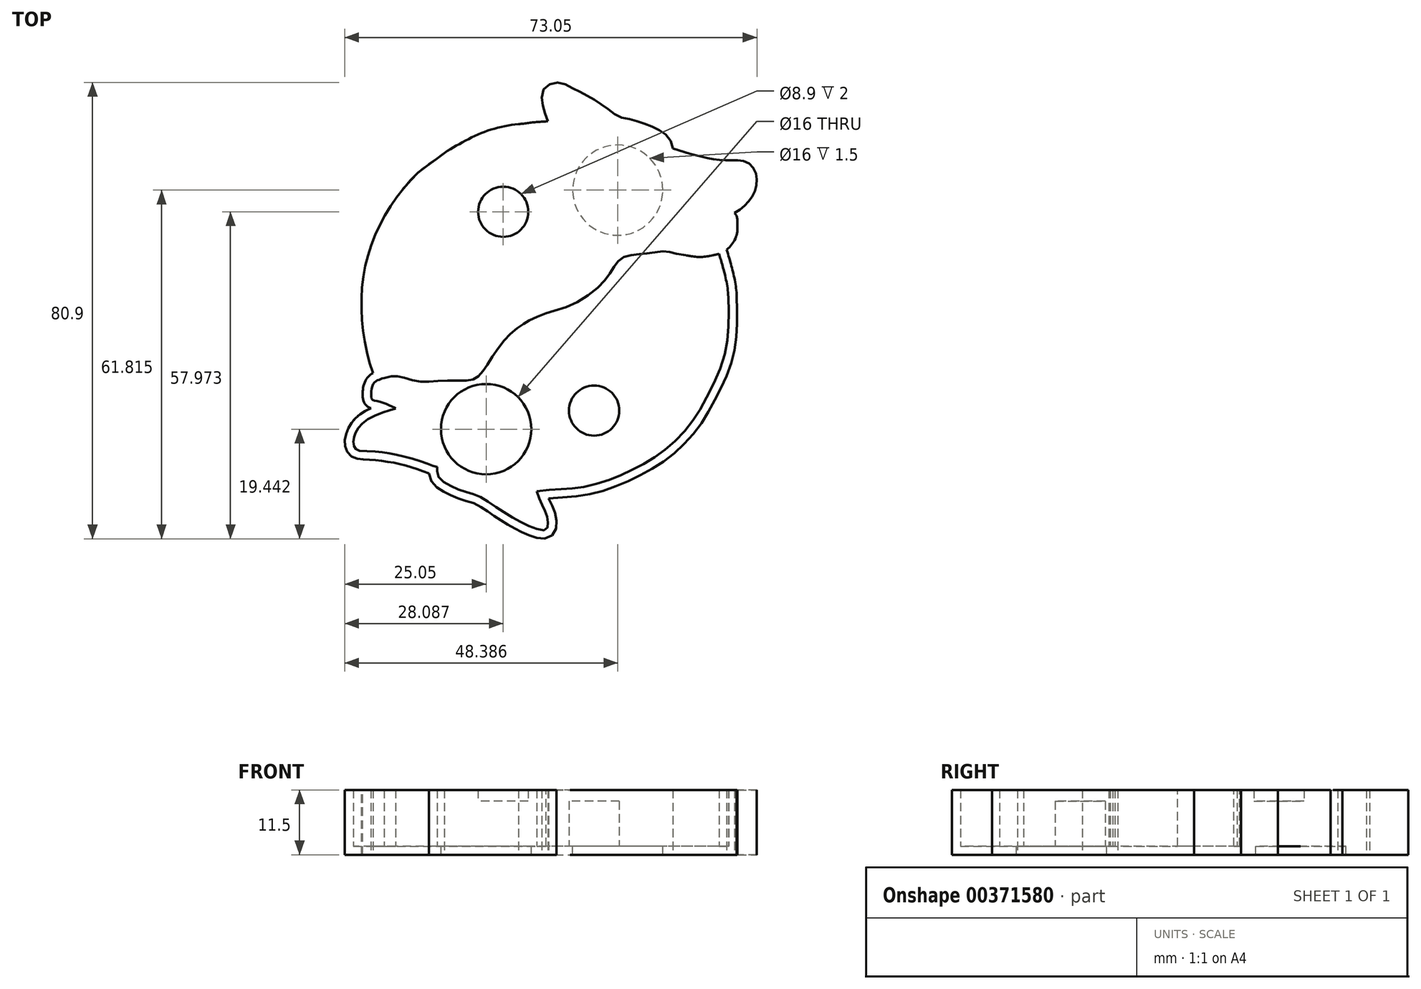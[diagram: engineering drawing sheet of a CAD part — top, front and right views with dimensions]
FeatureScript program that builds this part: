
annotation { "Feature Type Name" : "Feature", "Feature Type Description" : "" }
export const myFeature = defineFeature(function(context is Context, id is Id, definition is map)
    precondition{}
    {
        {
            var Q0;
            Q0=qCreatedBy(makeId("Top.planeOp"),FACE);
            var sketch = newSketch(context, id + "F0", { "sketchPlane" : qUnion([Q0])});
            skFitSpline(sketch, "E0", {"points": [v(-17.18, 27.16) * mm, v(-12.9, 29.6) * mm, v(-4.73, 31.98) * mm], "startDerivative": vector(7.12, 4.31) * mm, "endDerivative": vector(17.03, 1.2) * mm});
            skFitSpline(sketch, "E1", {"points": [v(-4.73, 31.98) * mm, v(-1.83, 32.34) * mm, v(1.14, 32.57) * mm, v(2.08, 32.77) * mm, v(2.37, 33.16) * mm, v(1.82, 34.3) * mm, v(1.14, 36.19) * mm, v(0.81, 37.69) * mm, v(0.81, 38.8) * mm, v(1.2, 39.19) * mm, v(2.11, 39.38) * mm, v(3.74, 38.67) * mm, v(5.54, 37.79) * mm, v(8.08, 36.35) * mm, v(10.88, 34.4) * mm, v(12.02, 33.45) * mm, v(13.23, 33.12) * mm, v(15.5, 32.67) * mm, v(18.57, 31.5) * mm, v(19.72, 30.91) * mm, v(20.53, 30.2) * mm, v(20.92, 29.38) * mm, v(21.13, 28.07) * mm], "startDerivative": vector(45.53, 6.4) * mm, "endDerivative": vector(4.07, -33.9) * mm});
            skFitSpline(sketch, "E2", {"points": [v(21.13, 28.07) * mm, v(23.45, 27.3) * mm, v(26.9, 26.34) * mm, v(30.59, 25.66) * mm, v(33.84, 25.62) * mm, v(34.62, 25.53) * mm, v(35.31, 25.1) * mm, v(35.84, 23.92) * mm, v(35.6, 22.12) * mm, v(34.4, 20.35) * mm, v(32.49, 18.96) * mm, v(30.62, 18.18) * mm, v(28.3, 17.5) * mm], "startDerivative": vector(24.49, -8.54) * mm, "endDerivative": vector(-26.98, -7.43) * mm});
            skFitSpline(sketch, "E3", {"points": [v(28.3, 17.5) * mm, v(30.16, 17.27) * mm, v(31.61, 16.98) * mm, v(32.35, 16.71) * mm, v(32.43, 15.93) * mm, v(32.27, 14.06) * mm, v(31.07, 12.4) * mm, v(30.18, 11.94) * mm], "startDerivative": vector(11.35, -1.19) * mm, "endDerivative": vector(-6.97, -2.69) * mm});
            skFitSpline(sketch, "E4", {"points": [v(30.18, 11.94) * mm, v(31.11, 9) * mm, v(32.3, 2.86) * mm], "startDerivative": vector(2.29, -6.25) * mm, "endDerivative": vector(0.47, -11.3) * mm});
            skFitSpline(sketch, "E5", {"points": [v(32.3, 2.86) * mm, v(32.3, -3.13) * mm, v(31.34, -8.57) * mm, v(28.44, -14.98) * mm, v(25.92, -19.2) * mm, v(22.47, -23.04) * mm, v(18.74, -25.9) * mm, v(14.64, -28.07) * mm, v(10.7, -29.73) * mm, v(6.04, -30.9) * mm, v(2.54, -31.18) * mm, v(-1.68, -31.6) * mm], "startDerivative": vector(1.57, -61.16) * mm, "endDerivative": vector(-51.86, -5.85) * mm});
            skFitSpline(sketch, "E6", {"points": [v(-1.68, -31.6) * mm, v(-0.99, -33.3) * mm, v(-0.3, -34.75) * mm, v(0.18, -36) * mm, v(0.34, -37.1) * mm, v(0.25, -38) * mm, v(-0.3, -38.49) * mm, v(-2, -38.16) * mm, v(-4.28, -37.15) * mm, v(-7.16, -35.5) * mm, v(-9.66, -33.84) * mm, v(-11.96, -32.44) * mm, v(-13.8, -31.85) * mm, v(-15.9, -31.1) * mm, v(-17.92, -30.06) * mm, v(-19.12, -28.9) * mm, v(-19.32, -27.87) * mm, v(-19.32, -27.3) * mm], "startDerivative": vector(10.96, -28.51) * mm, "endDerivative": vector(0.26, 15.5) * mm});
            skFitSpline(sketch, "E7", {"points": [v(-19.32, -27.3) * mm, v(-20.25, -27.01) * mm, v(-22.37, -26.23) * mm, v(-25.73, -25.26) * mm, v(-28.24, -24.8) * mm, v(-30.78, -24.53) * mm, v(-33.36, -24.32) * mm, v(-33.82, -24) * mm, v(-34.12, -23.44) * mm, v(-34.14, -22.43) * mm, v(-33.87, -21.44) * mm, v(-33.1, -20.12) * mm, v(-31.63, -18.86) * mm, v(-28.68, -17.52) * mm, v(-26.68, -16.92) * mm], "startDerivative": vector(-16.02, 4.34) * mm, "endDerivative": vector(23.79, 6.57) * mm});
            skFitSpline(sketch, "E8", {"points": [v(-26.68, -16.92) * mm, v(-27.85, -16.3) * mm, v(-30.13, -15.54) * mm, v(-30.85, -15.28) * mm, v(-31, -14.04) * mm, v(-30.69, -12.66) * mm, v(-30.04, -11.99) * mm, v(-29.4, -11.73) * mm, v(-28.7, -11.5) * mm], "startDerivative": vector(-7.77, 4.64) * mm, "endDerivative": vector(10.32, 1.26) * mm});
            skFitSpline(sketch, "E9", {"points": [v(-28.7, -11.5) * mm, v(-29.82, -8.42) * mm, v(-31, -2.52) * mm, v(-31.1, 4.58) * mm, v(-30.18, 9.65) * mm, v(-27.5, 16.2) * mm, v(-24.34, 20.86) * mm, v(-21.4, 24) * mm, v(-17.18, 27.16) * mm], "startDerivative": vector(-19.88, 53.95) * mm, "endDerivative": vector(33.85, 27.15) * mm});
            skSolve(sketch);
        }
        {
            var Q0;
            Q0=makeQuery(id+"F0.imprint","IMPRINT",FACE,{"disambiguationData":[TD([[makeQuery(id+"F0.imprint","IMPRINT",EDGE,{"derivedFrom":sQuery(id+"F0.wireOp",EDGE,"E0")}),-1.0]])]});
            extrude(context, id + "F1", {"entities" : qUnion([Q0]), "depth" : 10 * mm});
        }
        {
            var Q0;
            Q0=makeQuery(id+"F1.opExtrude","CAP_FACE",FACE,{"disambiguationData":[OSD([sQuery(id+"F0.wireOp",EDGE,"E0"),sQuery(id+"F0.wireOp",EDGE,"E1"),sQuery(id+"F0.wireOp",EDGE,"E2"),sQuery(id+"F0.wireOp",EDGE,"E3"),sQuery(id+"F0.wireOp",EDGE,"E4"),sQuery(id+"F0.wireOp",EDGE,"E5"),sQuery(id+"F0.wireOp",EDGE,"E6"),sQuery(id+"F0.wireOp",EDGE,"E7"),sQuery(id+"F0.wireOp",EDGE,"E8"),sQuery(id+"F0.wireOp",EDGE,"E9")])],"isStart":false});
            shell(context, id + "F2", {"entities" : qUnion([Q0]), "thickness" : 1.5 * mm, "oppositeDirection" : true});
        }
        {
            var Q0;
            Q0=makeQuery(id+"F2.opShell","OFFSET_FACE",FACE,{"disambiguationData":[OSD([sQuery(id+"F0.wireOp",EDGE,"E0"),sQuery(id+"F0.wireOp",EDGE,"E1"),sQuery(id+"F0.wireOp",EDGE,"E2"),sQuery(id+"F0.wireOp",EDGE,"E3"),sQuery(id+"F0.wireOp",EDGE,"E4"),sQuery(id+"F0.wireOp",EDGE,"E5"),sQuery(id+"F0.wireOp",EDGE,"E6"),sQuery(id+"F0.wireOp",EDGE,"E7"),sQuery(id+"F0.wireOp",EDGE,"E8"),sQuery(id+"F0.wireOp",EDGE,"E9")])]});
            var sketch = newSketch(context, id + "F3", { "sketchPlane" : qUnion([Q0])});
            skCircle(sketch, "E10", {"center": v(-7.6, 17.96) * mm, "radius": 4.45 * mm});
            skCircle(sketch, "E11", {"center": v(8.51, -17.28) * mm, "radius": 4.45 * mm});
            skSolve(sketch);
        }
        {
            var Q0;
            Q0=makeQuery(id+"F3.imprint","IMPRINT",FACE,{"disambiguationData":[TD([[makeQuery(id+"F3.imprint","IMPRINT",EDGE,{"derivedFrom":sQuery(id+"F3.wireOp",EDGE,"E10")}),1.0]])]});
            var Q1;
            Q1=makeQuery(id+"F3.imprint","IMPRINT",FACE,{"disambiguationData":[TD([[makeQuery(id+"F3.imprint","IMPRINT",EDGE,{"derivedFrom":sQuery(id+"F3.wireOp",EDGE,"E11")}),1.0]])]});
            extrude(context, id + "F4", {"entities" : qUnion([Q0, Q1]), "operationType" : NewBodyOperationType.ADD, "depth" : 8 * mm, "offsetDistance" : 25 * mm});
        }
        {
            var Q0;
            Q0=makeQuery(id+"F2.opShell","OFFSET_FACE",FACE,{"disambiguationData":[OSD([sQuery(id+"F0.wireOp",EDGE,"E0"),sQuery(id+"F0.wireOp",EDGE,"E1"),sQuery(id+"F0.wireOp",EDGE,"E2"),sQuery(id+"F0.wireOp",EDGE,"E3"),sQuery(id+"F0.wireOp",EDGE,"E4"),sQuery(id+"F0.wireOp",EDGE,"E5"),sQuery(id+"F0.wireOp",EDGE,"E6"),sQuery(id+"F0.wireOp",EDGE,"E7"),sQuery(id+"F0.wireOp",EDGE,"E8"),sQuery(id+"F0.wireOp",EDGE,"E9")])]});
            var sketch = newSketch(context, id + "F5", { "sketchPlane" : qUnion([Q0])});
            skFitSpline(sketch, "E12", {"points": [v(-28.7, -11.5) * mm, v(-26.96, -11.15) * mm, v(-25.5, -11.35) * mm, v(-23.05, -12.08) * mm, v(-20.6, -12.16) * mm, v(-17.42, -11.96) * mm, v(-14.3, -11.96) * mm, v(-12.7, -11.7) * mm, v(-11.44, -10.58) * mm, v(-10.33, -8.96) * mm, v(-8.28, -5.91) * mm, v(-6.35, -3.73) * mm, v(-4.24, -2.07) * mm, v(-2.82, -1.23) * mm, v(0, 0) * mm], "startDerivative": vector(28.4, 10.68) * mm, "endDerivative": vector(36.68, 13.75) * mm});
            skFitSpline(sketch, "E13.0", {"points": [v(-29.23, -10.1) * mm, v(-28.86, -9.96) * mm, v(-28.1, -9.74) * mm, v(-27.17, -9.63) * mm, v(-26.44, -9.65) * mm, v(-25.9, -9.71) * mm, v(-25.39, -9.83) * mm, v(-24.7, -10.03) * mm, v(-24, -10.26) * mm, v(-23.35, -10.47) * mm, v(-22.9, -10.58) * mm, v(-22.5, -10.65) * mm, v(-22.09, -10.7) * mm, v(-21.66, -10.7) * mm, v(-21.2, -10.69) * mm, v(-20.69, -10.66) * mm, v(-19.95, -10.6) * mm, v(-19.15, -10.55) * mm, v(-18.3, -10.5) * mm, v(-17.65, -10.47) * mm, v(-16.98, -10.45) * mm, v(-16.1, -10.45) * mm, v(-15.28, -10.46) * mm, v(-14.56, -10.47) * mm, v(-14.1, -10.46) * mm, v(-13.75, -10.44) * mm, v(-13.56, -10.41) * mm, v(-13.46, -10.38) * mm, v(-13.4, -10.36) * mm, v(-13.35, -10.34) * mm, v(-13.28, -10.3) * mm, v(-13.19, -10.23) * mm, v(-13.06, -10.12) * mm, v(-12.87, -9.95) * mm, v(-12.64, -9.69) * mm, v(-12.42, -9.4) * mm, v(-12.2, -9.1) * mm, v(-11.97, -8.74) * mm, v(-11.7, -8.32) * mm, v(-11.4, -7.84) * mm, v(-11.05, -7.3) * mm, v(-10.55, -6.55) * mm, v(-10.03, -5.77) * mm, v(-9.5, -5.03) * mm, v(-8.97, -4.34) * mm, v(-8.3, -3.54) * mm, v(-7.58, -2.8) * mm, v(-6.94, -2.24) * mm, v(-6.45, -1.84) * mm, v(-5.97, -1.47) * mm, v(-5.5, -1.12) * mm, v(-5.07, -0.82) * mm, v(-4.67, -0.55) * mm, v(-4.27, -0.3) * mm, v(-3.86, -0.07) * mm, v(-3.4, 0.16) * mm, v(-2.9, 0.4) * mm, v(-2.34, 0.66) * mm, v(-1.55, 1) * mm, v(-0.93, 1.25) * mm, v(-0.53, 1.4) * mm]});
            skFitSpline(sketch, "E14", {"points": [v(30.18, 11.94) * mm, v(28.48, 11.55) * mm, v(27.07, 11.46) * mm, v(25.7, 11.6) * mm, v(23.45, 12) * mm, v(21.15, 12.44) * mm, v(17.79, 12.07) * mm, v(14.12, 11.61) * mm, v(11.66, 10.22) * mm, v(9.94, 7.7) * mm, v(8.15, 5.63) * mm, v(5.13, 3.45) * mm, v(2.3, 2.23) * mm, v(-0.53, 1.4) * mm], "startDerivative": vector(-26.62, -8.93) * mm, "endDerivative": vector(-29.76, -11.2) * mm});
            skFitSpline(sketch, "E15.0", {"points": [v(30.66, 10.52) * mm, v(30.32, 10.4) * mm, v(29.82, 10.27) * mm, v(29.17, 10.14) * mm, v(28.7, 10.07) * mm, v(28.25, 10) * mm, v(27.8, 9.97) * mm, v(27.33, 9.95) * mm, v(26.87, 9.96) * mm, v(26.43, 10) * mm, v(26, 10.05) * mm, v(25.65, 10.1) * mm, v(25.37, 10.14) * mm, v(25.06, 10.19) * mm, v(24.65, 10.25) * mm, v(24.12, 10.34) * mm, v(23.67, 10.43) * mm, v(23.3, 10.5) * mm, v(22.94, 10.58) * mm, v(22.52, 10.69) * mm, v(22.07, 10.8) * mm, v(21.67, 10.88) * mm, v(21.3, 10.93) * mm, v(20.93, 10.95) * mm, v(20.47, 10.92) * mm, v(19.95, 10.86) * mm, v(19.37, 10.78) * mm, v(18.74, 10.68) * mm, v(18.18, 10.6) * mm, v(17.71, 10.55) * mm, v(17.26, 10.5) * mm, v(16.7, 10.46) * mm, v(16.08, 10.4) * mm, v(15.5, 10.34) * mm, v(14.96, 10.26) * mm, v(14.48, 10.16) * mm, v(14.07, 10.04) * mm, v(13.57, 9.83) * mm, v(13.14, 9.56) * mm, v(12.82, 9.27) * mm, v(12.65, 9.08) * mm, v(12.47, 8.87) * mm, v(12.24, 8.55) * mm, v(11.96, 8.11) * mm, v(11.66, 7.63) * mm, v(11.35, 7.12) * mm, v(11.01, 6.6) * mm, v(10.65, 6.1) * mm, v(10.26, 5.63) * mm, v(9.7, 5.03) * mm, v(8.93, 4.3) * mm, v(7.86, 3.45) * mm, v(6.7, 2.64) * mm, v(5.53, 1.93) * mm, v(4.37, 1.37) * mm, v(3.2, 0.93) * mm, v(2, 0.58) * mm, v(0.86, 0.28) * mm, v(0.24, 0.1) * mm, v(0, 0) * mm]});
            skSolve(sketch);
        }
        {
            var Q0;
            {var subQ6=sQuery(id+"F5.wireOp",EDGE,"E12");Q0=makeQuery(id+"F5.imprint","IMPRINT",FACE,{"disambiguationData":[TD([[makeQuery(id+"F5.imprint","IMPRINT",EDGE,{"derivedFrom":subQ6}),1.0]])]});}
            extrude(context, id + "F6", {"entities" : qUnion([Q0]), "operationType" : NewBodyOperationType.ADD, "depth" : 10 * mm});
        }
        {
            var Q0;
            {var subQ0=sQuery(id+"F0.wireOp",EDGE,"E9");var subQ1=sQuery(id+"F0.wireOp",EDGE,"E3");var subQ2=sQuery(id+"F0.wireOp",EDGE,"E2");var subQ3=sQuery(id+"F0.wireOp",EDGE,"E1");var subQ4=sQuery(id+"F0.wireOp",EDGE,"E0");Q0=makeQuery(id+"F6.boolean.opBoolean","SPLIT",FACE,{"disambiguationData":[TD([makeQuery(id+"F2.opShell","OFFSET_FACE",FACE,{"disambiguationData":[OSD([subQ4])]})])],"derivedFrom":makeQuery(id+"F2.opShell","OFFSET_FACE",FACE,{"disambiguationData":[OSD([subQ4,subQ3,subQ2,subQ1,sQuery(id+"F0.wireOp",EDGE,"E4"),sQuery(id+"F0.wireOp",EDGE,"E5"),sQuery(id+"F0.wireOp",EDGE,"E6"),sQuery(id+"F0.wireOp",EDGE,"E7"),sQuery(id+"F0.wireOp",EDGE,"E8"),subQ0])]})});}
            var sketch = newSketch(context, id + "F7", { "sketchPlane" : qUnion([Q0])});
            skCircle(sketch, "E16", {"center": v(12.7, 21.8) * mm, "radius": 8 * mm});
            skCircle(sketch, "E17", {"center": v(-10.63, -20.57) * mm, "radius": 8 * mm});
            skSolve(sketch);
        }
        {
            var Q0;
            Q0 = qSketchRegion(id + "F7", true);
            extrude(context, id + "F8", {"entities" : qUnion([Q0]), "operationType" : NewBodyOperationType.REMOVE, "oppositeDirection" : true, "depth" : 1.5 * mm});
        }
    });
